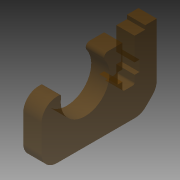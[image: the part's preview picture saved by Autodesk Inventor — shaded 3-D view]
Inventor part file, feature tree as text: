
AUTODESK INVENTOR PART (.ipt)
format: ipt  version: 2014 SP1 (Build 180222100, 222)  size: 111,104 bytes
history: native  units: mm
features: extrude x1, sketch x1
ambient origin geometry x8: Origin, YZ Plane, XZ Plane, XY Plane, X Axis, Y Axis, Z Axis, Center Point
bodies: Solid1 (feature_tree)
feature tree (2):
  extrude  "Extrusion1"  [1 undecoded]
  sketch  "Sketch1"  dims[d0=4.7625mm d1=0.0mm]
note: 1 required parameter value undecoded (feature->parameter linkage not recoverable at this tier; creation-order binding heuristic only, values carry confidence <= 0.55)
